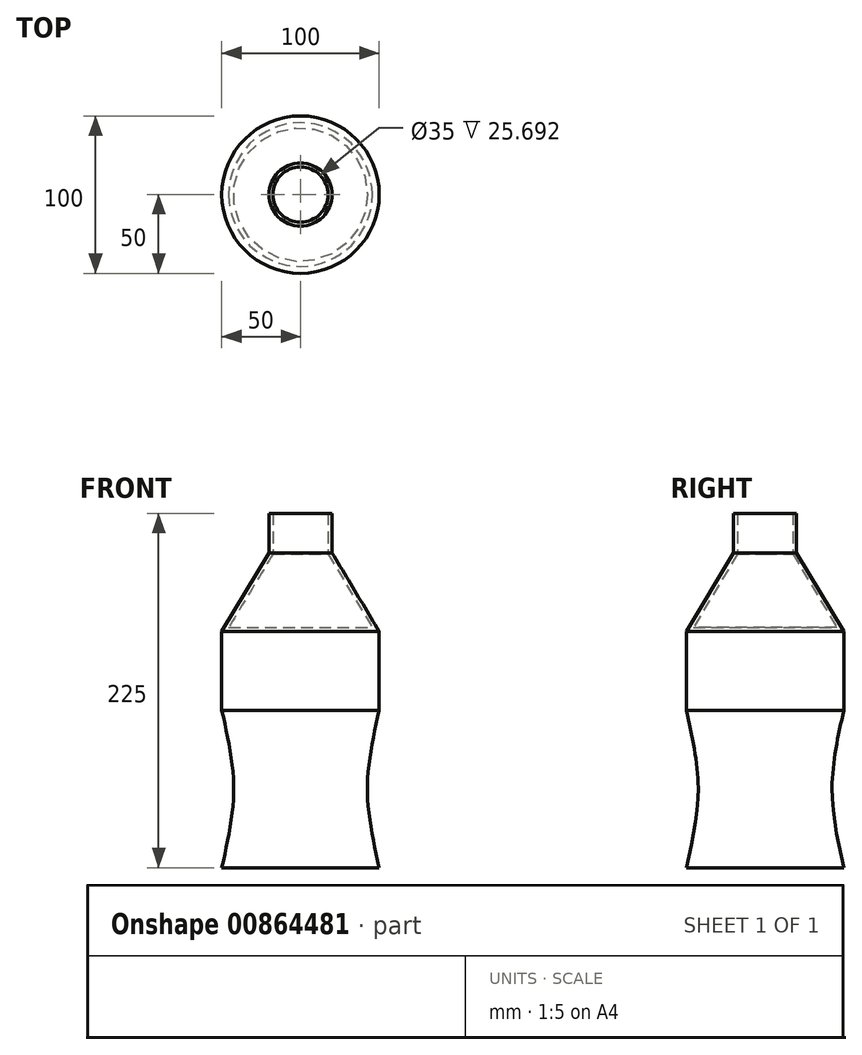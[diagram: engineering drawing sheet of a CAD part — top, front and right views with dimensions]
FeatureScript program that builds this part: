
annotation { "Feature Type Name" : "Feature", "Feature Type Description" : "" }
export const myFeature = defineFeature(function(context is Context, id is Id, definition is map)
    precondition{}
    {
        {
            var Q0;
            Q0=qCreatedBy(makeId("Top.planeOp"),FACE);
            var sketch = newSketch(context, id + "F0", { "sketchPlane" : qUnion([Q0])});
            skCircle(sketch, "E0", {"center": v(0, 0) * mm, "radius": 50 * mm});
            skSolve(sketch);
        }
        {
            var Q0;
            Q0=qCreatedBy(makeId("Top.planeOp"),FACE);
            cPlane(context, id + "F1", {"entities" : qUnion([Q0]), "cplaneType" : CPlaneType.OFFSET, "offset" : 50 * mm, "width" : 150 * mm, "height" : 150 * mm});
        }
        {
            var Q0;
            Q0=qCreatedBy(makeId("Top.planeOp"),FACE);
            cPlane(context, id + "F2", {"entities" : qUnion([Q0]), "cplaneType" : CPlaneType.OFFSET, "offset" : 100 * mm, "width" : 150 * mm, "height" : 150 * mm});
        }
        {
            var Q0;
            Q0=qCreatedBy(makeId("Top.planeOp"),FACE);
            cPlane(context, id + "F3", {"entities" : qUnion([Q0]), "cplaneType" : CPlaneType.OFFSET, "offset" : 150 * mm, "width" : 150 * mm, "height" : 150 * mm});
        }
        {
            var Q0;
            Q0=qCreatedBy(id+"F2.planeOp",FACE);
            var sketch = newSketch(context, id + "F4", { "sketchPlane" : qUnion([Q0])});
            skCircle(sketch, "E1", {"center": v(0, 0) * mm, "radius": 50 * mm});
            skSolve(sketch);
        }
        {
            var Q0;
            Q0=qCreatedBy(id+"F3.planeOp",FACE);
            var sketch = newSketch(context, id + "F5", { "sketchPlane" : qUnion([Q0])});
            skCircle(sketch, "E2", {"center": v(0, 0) * mm, "radius": 50 * mm});
            skSolve(sketch);
        }
        {
            var Q0;
            Q0=qCreatedBy(id+"F1.planeOp",FACE);
            var sketch = newSketch(context, id + "F6", { "sketchPlane" : qUnion([Q0])});
            skCircle(sketch, "E3", {"center": v(0, 0) * mm, "radius": 42.5 * mm});
            skSolve(sketch);
        }
        {
            var Q0;
            Q0=qCreatedBy(makeId("Top.planeOp"),FACE);
            cPlane(context, id + "F7", {"entities" : qUnion([Q0]), "cplaneType" : CPlaneType.OFFSET, "offset" : 200 * mm, "width" : 150 * mm, "height" : 150 * mm});
        }
        {
            var Q0;
            Q0=qCreatedBy(id+"F7.planeOp",FACE);
            var sketch = newSketch(context, id + "F8", { "sketchPlane" : qUnion([Q0])});
            skCircle(sketch, "E4", {"center": v(0, 0) * mm, "radius": 20 * mm});
            skSolve(sketch);
        }
        {
            var Q0;
            Q0=makeQuery(id+"F0.imprint","IMPRINT",FACE,{"disambiguationData":[TD([[makeQuery(id+"F0.imprint","IMPRINT",EDGE,{"derivedFrom":sQuery(id+"F0.wireOp",EDGE,"E0")}),1.0]])]});
            var Q1;
            Q1=makeQuery(id+"F6.imprint","IMPRINT",FACE,{"disambiguationData":[TD([[makeQuery(id+"F6.imprint","IMPRINT",EDGE,{"derivedFrom":sQuery(id+"F6.wireOp",EDGE,"E3")}),1.0]])]});
            var Q2;
            Q2=makeQuery(id+"F4.imprint","IMPRINT",FACE,{"disambiguationData":[TD([[makeQuery(id+"F4.imprint","IMPRINT",EDGE,{"derivedFrom":sQuery(id+"F4.wireOp",EDGE,"E1")}),1.0]])]});
            loft(context, id + "F9", {"sheetProfilesArray" : [{ "sheetProfileEntities" : qUnion([Q0]) }, { "sheetProfileEntities" : qUnion([Q1]) }, { "sheetProfileEntities" : qUnion([Q2]) }]});
        }
        {
            var Q0;
            Q0=makeQuery(id+"F9.opLoft","CAP_FACE",FACE,{"disambiguationData":[OSD([makeQuery(id+"F4.imprint","IMPRINT",FACE,{"disambiguationData":[TD([[makeQuery(id+"F4.imprint","IMPRINT",EDGE,{"derivedFrom":sQuery(id+"F4.wireOp",EDGE,"E1")}),1.0]])]})])],"isStart":true});
            extrude(context, id + "F10", {"entities" : qUnion([Q0]), "operationType" : NewBodyOperationType.ADD, "depth" : 50 * mm, "offsetDistance" : 25 * mm});
        }
        {
            var Q0;
            Q0=makeQuery(id+"F5.imprint","IMPRINT",FACE,{"disambiguationData":[TD([[makeQuery(id+"F5.imprint","IMPRINT",EDGE,{"derivedFrom":sQuery(id+"F5.wireOp",EDGE,"E2")}),1.0]])]});
            var Q1;
            Q1=makeQuery(id+"F8.imprint","IMPRINT",FACE,{"disambiguationData":[TD([[makeQuery(id+"F8.imprint","IMPRINT",EDGE,{"derivedFrom":sQuery(id+"F8.wireOp",EDGE,"E4")}),1.0]])]});
            loft(context, id + "F11", {"sheetProfilesArray" : [{ "sheetProfileEntities" : qUnion([Q0]) }, { "sheetProfileEntities" : qUnion([Q1]) }]});
        }
        {
            var Q0;
            Q0=makeQuery(id+"F11.opLoft","CAP_FACE",FACE,{"disambiguationData":[OSD([makeQuery(id+"F8.imprint","IMPRINT",FACE,{"disambiguationData":[TD([[makeQuery(id+"F8.imprint","IMPRINT",EDGE,{"derivedFrom":sQuery(id+"F8.wireOp",EDGE,"E4")}),1.0]])]})])],"isStart":true});
            extrude(context, id + "F12", {"entities" : qUnion([Q0]), "operationType" : NewBodyOperationType.ADD, "depth" : 25 * mm, "offsetDistance" : 25 * mm});
        }
        {
            var Q0;
            Q0=makeQuery(id+"F12.opExtrude","CAP_FACE",FACE,{"disambiguationData":[OSD([makeQuery(id+"F8.imprint","IMPRINT",FACE,{"disambiguationData":[TD([[makeQuery(id+"F8.imprint","IMPRINT",EDGE,{"derivedFrom":sQuery(id+"F8.wireOp",EDGE,"E4")}),1.0]])]})])],"isStart":false});
            shell(context, id + "F13", {"entities" : qUnion([Q0]), "thickness" : 2.5 * mm});
        }
    });
